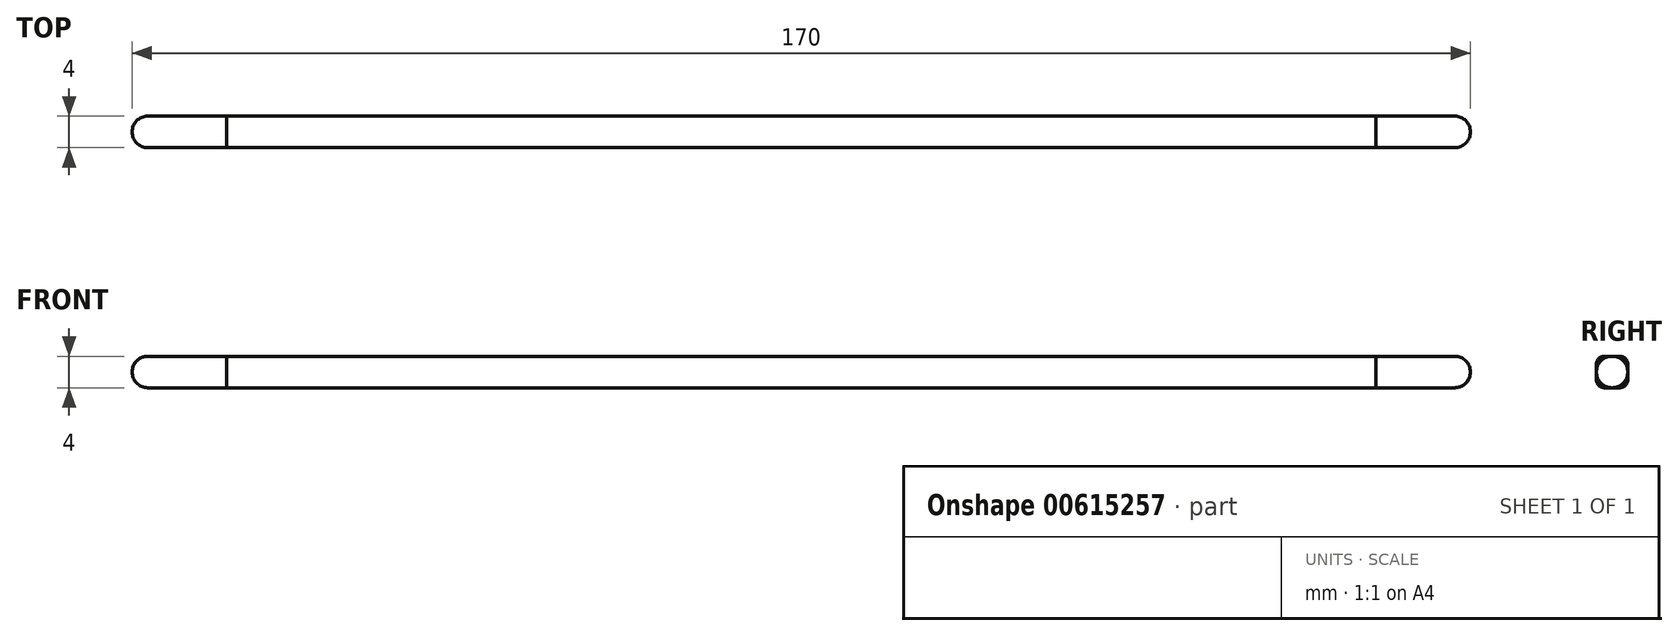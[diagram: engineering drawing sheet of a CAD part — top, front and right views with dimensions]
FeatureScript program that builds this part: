
annotation { "Feature Type Name" : "Feature", "Feature Type Description" : "" }
export const myFeature = defineFeature(function(context is Context, id is Id, definition is map)
    precondition{}
    {
        {
            var Q0;
            Q0=qCreatedBy(makeId("Top.planeOp"),FACE);
            var sketch = newSketch(context, id + "F0", { "sketchPlane" : qUnion([Q0])});
            skLineSegment(sketch, "E0.bottom", {"start": v(73, -2) * mm, "end": v(-73, -2) * mm});
            skLineSegment(sketch, "E0.top", {"start": v(73, 2) * mm, "end": v(-73, 2) * mm});
            skLineSegment(sketch, "E0.left", {"start": v(73, -2) * mm, "end": v(73, 2) * mm});
            skLineSegment(sketch, "E0.right", {"start": v(-73, -2) * mm, "end": v(-73, 2) * mm});
            skPoint(sketch, "E0.middle", {"position": v(0, 0) * mm});
            skSolve(sketch);
        }
        {
            var Q0;
            Q0=makeQuery(id+"F0.imprint","IMPRINT",FACE,{"disambiguationData":[TD([[makeQuery(id+"F0.imprint","IMPRINT",EDGE,{"derivedFrom":sQuery(id+"F0.wireOp",EDGE,"E0.bottom")}),-1.0]])]});
            extrude(context, id + "F1", {"entities" : qUnion([Q0]), "depth" : 4 * mm, "offsetDistance" : 25 * mm});
        }
        {
            var Q0;
            Q0=makeQuery(id+"F1.opExtrude","SWEPT_FACE",FACE,{"disambiguationData":[OSD([sQuery(id+"F0.wireOp",EDGE,"E0.right")])]});
            var sketch = newSketch(context, id + "F2", { "sketchPlane" : qUnion([Q0])});
            skLineSegment(sketch, "E1", {"start": v(-2, 0) * mm, "end": v(2, 4) * mm, "construction": true});
            skCircle(sketch, "E2", {"center": v(0, 2) * mm, "radius": 2 * mm});
            skSolve(sketch);
        }
        {
            var Q0;
            {var subQ0=sQuery(id+"F2.wireOp",EDGE,"E2");var subQ1=sQuery(id+"F0.wireOp",EDGE,"E0.right");var subQ2=makeQuery(id+"F2.imprint","INTERSECT",VERTEX,{"derivedFrom":[makeQuery(id+"F1.opExtrude","CAP_EDGE",EDGE,{"disambiguationData":[OSD([subQ1])],"isStart":false}),subQ0]});Q0=makeQuery(id+"F2.imprint","IMPRINT",FACE,{"disambiguationData":[TD([[makeQuery(id+"F2.imprint","IMPRINT",EDGE,{"disambiguationData":[TD([[subQ2,1.0]])],"derivedFrom":subQ0}),1.0]])]});}
            extrude(context, id + "F3", {"entities" : qUnion([Q0]), "operationType" : NewBodyOperationType.ADD, "depth" : 12 * mm, "offsetDistance" : 25 * mm});
        }
        {
            var Q0;
            Q0=makeQuery(id+"F3.opExtrude","CAP_FACE",FACE,{"disambiguationData":[OSD([sQuery(id+"F2.wireOp",EDGE,"E2")])],"isStart":false});
            fillet(context, id + "F4", {"entities" : qUnion([Q0]), "radius" : 2 * mm, "tangentPropagation" : true, "allowEdgeOverflow" : false});
        }
        {
            var Q0;
            Q0=makeQuery(id+"F1.opExtrude","SWEPT_FACE",FACE,{"disambiguationData":[OSD([sQuery(id+"F0.wireOp",EDGE,"E0.left")])]});
            var sketch = newSketch(context, id + "F5", { "sketchPlane" : qUnion([Q0])});
            skLineSegment(sketch, "E3", {"start": v(-2, 0) * mm, "end": v(2, 4) * mm, "construction": true});
            skCircle(sketch, "E4", {"center": v(0, 2) * mm, "radius": 2 * mm});
            skSolve(sketch);
        }
        {
            var Q0;
            {var subQ0=sQuery(id+"F5.wireOp",EDGE,"E4");var subQ1=sQuery(id+"F0.wireOp",EDGE,"E0.left");var subQ2=makeQuery(id+"F5.imprint","INTERSECT",VERTEX,{"derivedFrom":[makeQuery(id+"F1.opExtrude","CAP_EDGE",EDGE,{"disambiguationData":[OSD([subQ1])],"isStart":false}),subQ0]});Q0=makeQuery(id+"F5.imprint","IMPRINT",FACE,{"disambiguationData":[TD([[makeQuery(id+"F5.imprint","IMPRINT",EDGE,{"disambiguationData":[TD([[subQ2,1.0]])],"derivedFrom":subQ0}),1.0]])]});}
            extrude(context, id + "F6", {"entities" : qUnion([Q0]), "operationType" : NewBodyOperationType.ADD, "depth" : 12 * mm, "offsetDistance" : 25 * mm});
        }
        {
            var Q0;
            Q0=makeQuery(id+"F6.opExtrude","CAP_FACE",FACE,{"disambiguationData":[OSD([sQuery(id+"F5.wireOp",EDGE,"E4")])],"isStart":false});
            fillet(context, id + "F7", {"entities" : qUnion([Q0]), "radius" : 2 * mm, "tangentPropagation" : true, "allowEdgeOverflow" : false});
        }
        {
            var Q0;
            Q0=makeQuery(id+"F1.opExtrude","CAP_EDGE",EDGE,{"disambiguationData":[OSD([sQuery(id+"F0.wireOp",EDGE,"E0.bottom")])],"isStart":false});
            var Q1;
            Q1=makeQuery(id+"F1.opExtrude","CAP_EDGE",EDGE,{"disambiguationData":[OSD([sQuery(id+"F0.wireOp",EDGE,"E0.bottom")])],"isStart":true});
            var Q2;
            Q2=makeQuery(id+"F1.opExtrude","CAP_EDGE",EDGE,{"disambiguationData":[OSD([sQuery(id+"F0.wireOp",EDGE,"E0.top")])],"isStart":true});
            var Q3;
            Q3=makeQuery(id+"F1.opExtrude","CAP_EDGE",EDGE,{"disambiguationData":[OSD([sQuery(id+"F0.wireOp",EDGE,"E0.top")])],"isStart":false});
            fillet(context, id + "F8", {"entities" : qUnion([Q0, Q1, Q2, Q3]), "radius" : 1 * mm, "tangentPropagation" : true, "allowEdgeOverflow" : false});
        }
    });
